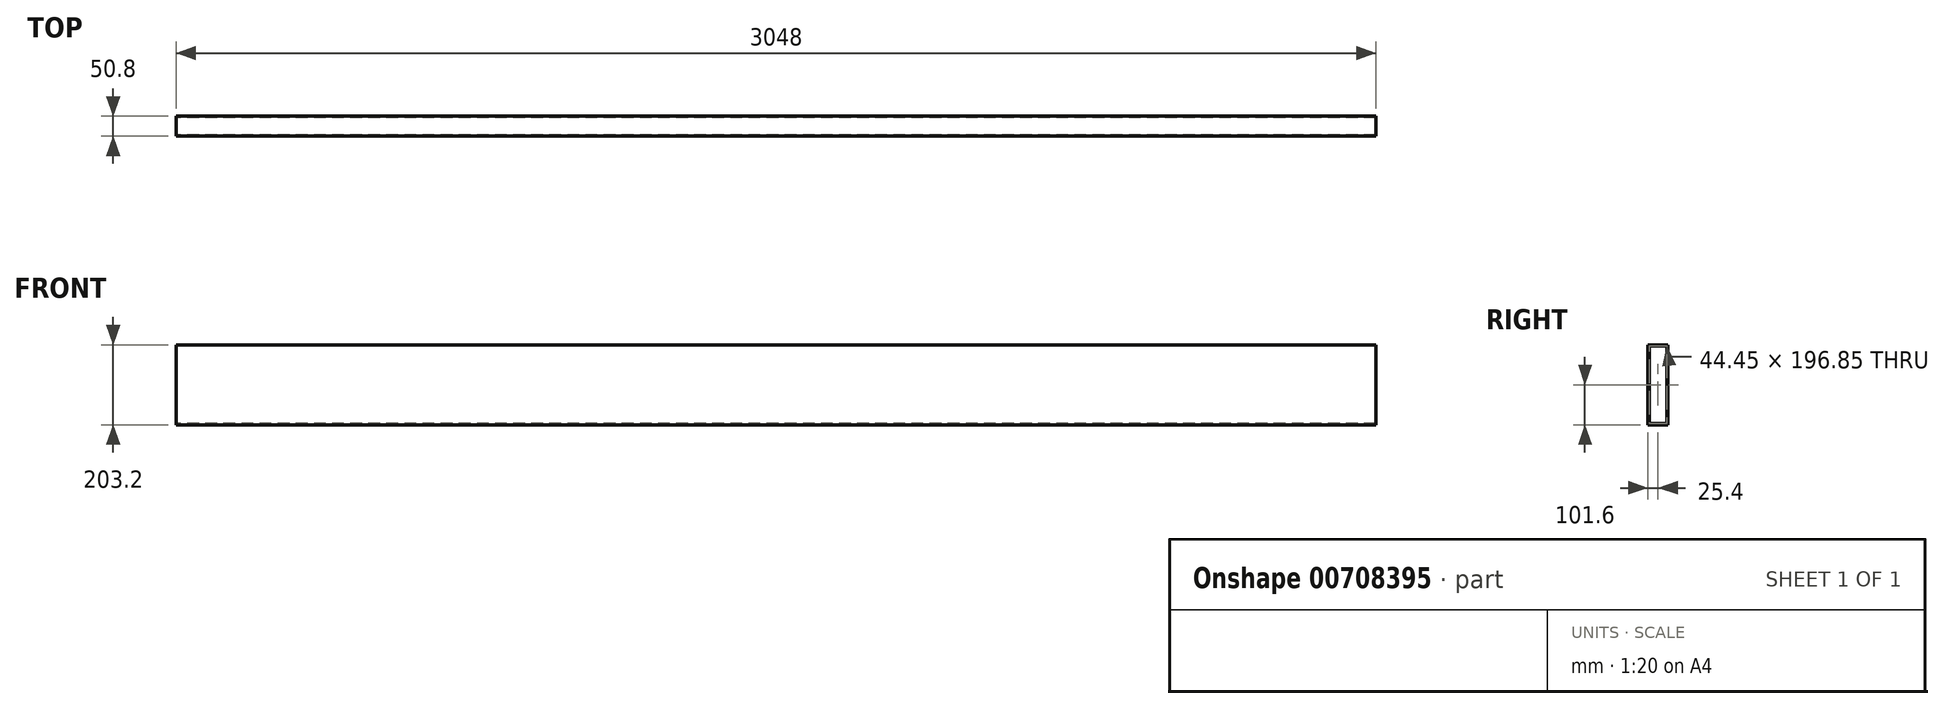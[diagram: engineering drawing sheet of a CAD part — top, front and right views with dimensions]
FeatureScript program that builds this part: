
annotation { "Feature Type Name" : "Feature", "Feature Type Description" : "" }
export const myFeature = defineFeature(function(context is Context, id is Id, definition is map)
    precondition{}
    {
        {
            var Q0;
            Q0=qCreatedBy(makeId("Right.planeOp"),FACE);
            var sketch = newSketch(context, id + "F0", { "sketchPlane" : qUnion([Q0])});
            skLineSegment(sketch, "E0.bottom", {"start": v(0, 0) * mm, "end": v(50.8, 0) * mm});
            skLineSegment(sketch, "E0.top", {"start": v(0, 203.2) * mm, "end": v(50.8, 203.2) * mm});
            skLineSegment(sketch, "E0.left", {"start": v(0, 0) * mm, "end": v(0, 203.2) * mm});
            skLineSegment(sketch, "E0.right", {"start": v(50.8, 0) * mm, "end": v(50.8, 203.2) * mm});
            skLineSegment(sketch, "E1.0", {"start": v(47.63, 3.17) * mm, "end": v(47.62, 200.03) * mm});
            skLineSegment(sketch, "E1.1", {"start": v(3.17, 3.17) * mm, "end": v(47.63, 3.17) * mm});
            skLineSegment(sketch, "E1.2", {"start": v(3.17, 3.17) * mm, "end": v(3.17, 200.03) * mm});
            skLineSegment(sketch, "E1.3", {"start": v(3.17, 200.03) * mm, "end": v(47.62, 200.03) * mm});
            skSolve(sketch);
        }
        {
            var Q0;
            Q0=makeQuery(id+"F0.imprint","IMPRINT",FACE,{"disambiguationData":[TD([[makeQuery(id+"F0.imprint","IMPRINT",EDGE,{"derivedFrom":sQuery(id+"F0.wireOp",EDGE,"E0.bottom")}),1.0]])]});
            extrude(context, id + "F1", {"entities" : qUnion([Q0]), "depth" : 3048 * mm, "offsetDistance" : 25.4 * mm});
        }
    });
